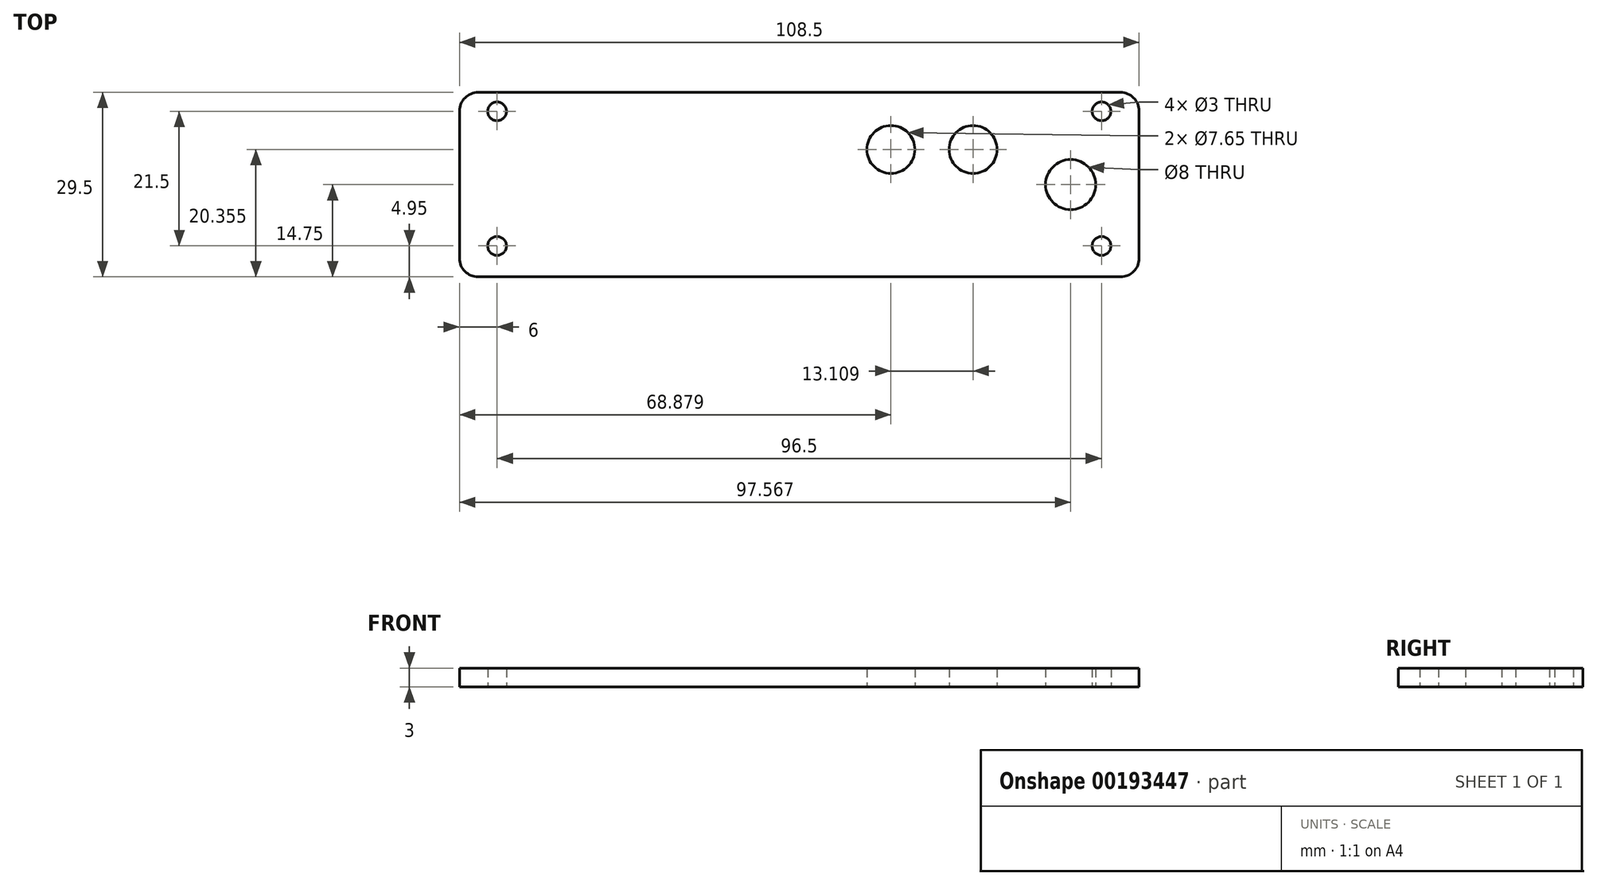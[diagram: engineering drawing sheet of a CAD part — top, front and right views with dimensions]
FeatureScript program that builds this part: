
annotation { "Feature Type Name" : "Feature", "Feature Type Description" : "" }
export const myFeature = defineFeature(function(context is Context, id is Id, definition is map)
    precondition{}
    {
        {
            var Q0;
            Q0=qCreatedBy(makeId("Top.planeOp"),FACE);
            var sketch = newSketch(context, id + "F0", { "sketchPlane" : qUnion([Q0])});
            skLineSegment(sketch, "E0.bottom", {"start": v(51.25, 14.75) * mm, "end": v(-51.25, 14.75) * mm});
            skLineSegment(sketch, "E0.top", {"start": v(51.25, -14.75) * mm, "end": v(-51.25, -14.75) * mm});
            skLineSegment(sketch, "E0.left", {"start": v(54.25, 11.75) * mm, "end": v(54.25, -11.75) * mm});
            skLineSegment(sketch, "E0.right", {"start": v(-54.25, 11.75) * mm, "end": v(-54.25, -11.75) * mm});
            skPoint(sketch, "E0.middle", {"position": v(0, 0) * mm});
            skCircle(sketch, "E1", {"center": v(-48.25, 11.7) * mm, "radius": 1.5 * mm});
            skCircle(sketch, "E2.MirrorC", {"center": v(48.25, 11.7) * mm, "radius": 1.5 * mm});
            skLineSegment(sketch, "E3", {"start": v(-54.25, 0) * mm, "end": v(54.25, 0) * mm});
            skCircle(sketch, "E4", {"center": v(-48.25, -9.8) * mm, "radius": 1.5 * mm});
            skCircle(sketch, "E5.MirrorC", {"center": v(48.25, -9.8) * mm, "radius": 1.5 * mm});
            skPoint(sketch, "E6.visualSharp", {"position": v(-54.25, 14.75) * mm});
            skArc(sketch, "E6.filletArc", {"start": v(-51.25, 14.75) * mm, "mid": v(-53.37, 13.87) * mm, "end": v(-54.25, 11.75) * mm});
            skPoint(sketch, "E7.visualSharp", {"position": v(54.25, 14.75) * mm});
            skArc(sketch, "E7.filletArc", {"start": v(54.25, 11.75) * mm, "mid": v(53.37, 13.87) * mm, "end": v(51.25, 14.75) * mm});
            skPoint(sketch, "E8.visualSharp", {"position": v(-54.25, -14.75) * mm});
            skArc(sketch, "E8.filletArc", {"start": v(-54.25, -11.75) * mm, "mid": v(-53.37, -13.87) * mm, "end": v(-51.25, -14.75) * mm});
            skPoint(sketch, "E9.visualSharp", {"position": v(54.25, -14.75) * mm});
            skArc(sketch, "E9.filletArc", {"start": v(51.25, -14.75) * mm, "mid": v(53.37, -13.87) * mm, "end": v(54.25, -11.75) * mm});
            skCircle(sketch, "E10", {"center": v(14.63, 5.6) * mm, "radius": 3.83 * mm});
            skCircle(sketch, "E11", {"center": v(27.74, 5.6) * mm, "radius": 3.83 * mm});
            skCircle(sketch, "E12", {"center": v(43.32, 0) * mm, "radius": 4 * mm});
            skSolve(sketch);
        }
        {
            var Q0;
            Q0=makeQuery(id+"F0.imprint","IMPRINT",FACE,{"disambiguationData":[TD([[makeQuery(id+"F0.imprint","IMPRINT",EDGE,{"derivedFrom":sQuery(id+"F0.wireOp",EDGE,"E0.top")}),-1.0]])]});
            var Q1;
            Q1=makeQuery(id+"F0.imprint","IMPRINT",FACE,{"disambiguationData":[TD([[makeQuery(id+"F0.imprint","IMPRINT",EDGE,{"derivedFrom":sQuery(id+"F0.wireOp",EDGE,"E0.bottom")}),1.0]])]});
            extrude(context, id + "F1", {"entities" : qUnion([Q0, Q1]), "depth" : 3 * mm});
        }
    });
